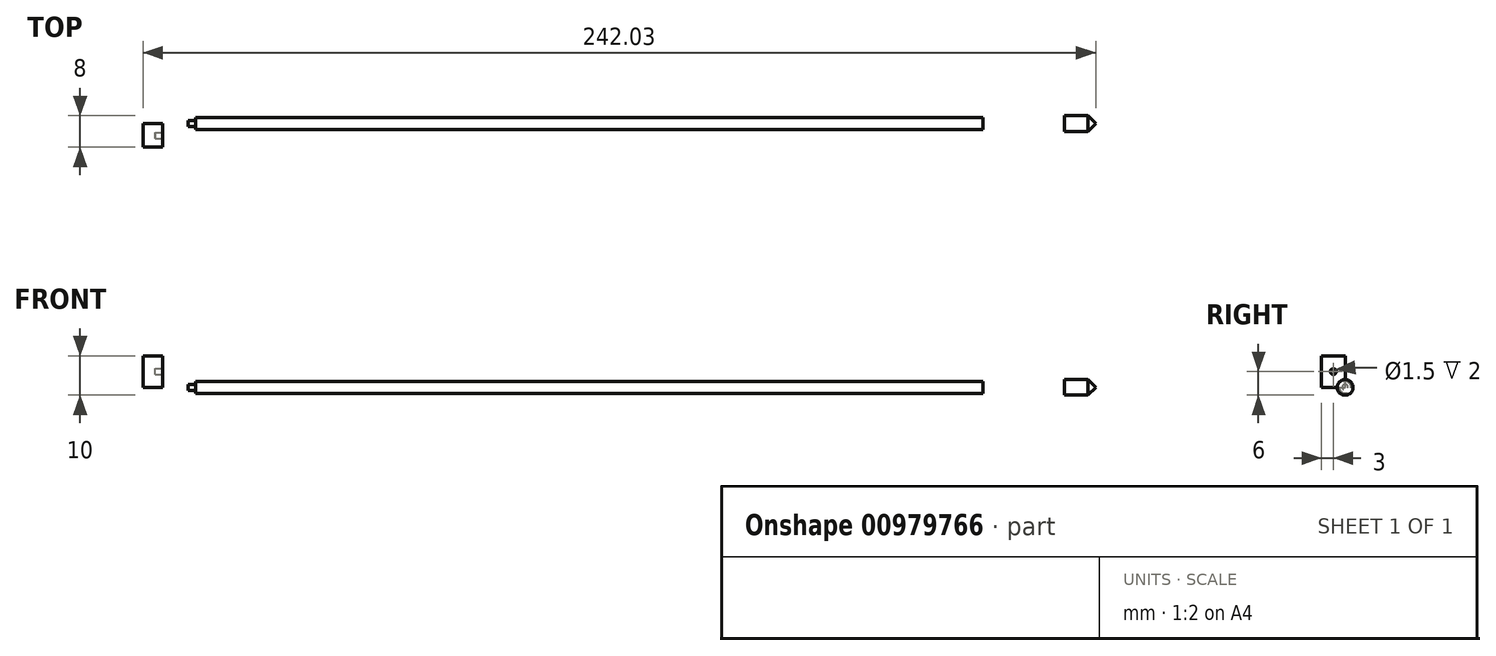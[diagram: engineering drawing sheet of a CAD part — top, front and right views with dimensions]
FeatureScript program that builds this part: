
annotation { "Feature Type Name" : "Feature", "Feature Type Description" : "" }
export const myFeature = defineFeature(function(context is Context, id is Id, definition is map)
    precondition{}
    {
        {
            var Q0;
            Q0=qCreatedBy(makeId("Front.planeOp"),FACE);
            var sketch = newSketch(context, id + "F0", { "sketchPlane" : qUnion([Q0])});
            skLineSegment(sketch, "E0.bottom", {"start": v(0, 0) * mm, "end": v(5, 0) * mm});
            skLineSegment(sketch, "E0.top", {"start": v(0, 8) * mm, "end": v(5, 8) * mm});
            skLineSegment(sketch, "E0.left", {"start": v(0, 0) * mm, "end": v(0, 8) * mm});
            skLineSegment(sketch, "E0.right", {"start": v(5, 0) * mm, "end": v(5, 8) * mm});
            skSolve(sketch);
        }
        {
            var Q0;
            Q0 = qSketchRegion(id + "F0", true);
            extrude(context, id + "F1", {"entities" : qUnion([Q0]), "depth" : 6 * mm, "offsetDistance" : 25 * mm});
        }
        {
            var Q0;
            Q0=qCreatedBy(makeId("Front.planeOp"),FACE);
            var sketch = newSketch(context, id + "F2", { "sketchPlane" : qUnion([Q0])});
            skLineSegment(sketch, "E1.bottom", {"start": v(13.38, 0) * mm, "end": v(213.38, 0) * mm});
            skLineSegment(sketch, "E1.top", {"start": v(13.38, 1.5) * mm, "end": v(213.38, 1.5) * mm});
            skLineSegment(sketch, "E1.left", {"start": v(13.38, 0) * mm, "end": v(13.38, 1.5) * mm});
            skLineSegment(sketch, "E1.right", {"start": v(213.38, 0) * mm, "end": v(213.38, 1.5) * mm});
            skSolve(sketch);
        }
        {
            var Q0;
            Q0 = qSketchRegion(id + "F2", true);
            var Q1;
            Q1=sQuery(id+"F2.wireOp",EDGE,"E1.bottom");
            revolve(context, id + "F3", {"surfaceOperationType" : NewSurfaceOperationType.NEW, "entities" : qUnion([Q0]), "axis" : qUnion([Q1]), "revolveType" : RevolveType.FULL});
        }
        {
            var Q0;
            Q0=makeQuery(id+"F3.opRevolve","SWEPT_FACE",FACE,{"disambiguationData":[OSD([sQuery(id+"F2.wireOp",EDGE,"E1.left")])]});
            var sketch = newSketch(context, id + "F4", { "sketchPlane" : qUnion([Q0])});
            skCircle(sketch, "E2", {"center": v(0, 0) * mm, "radius": 0.75 * mm});
            skSolve(sketch);
        }
        {
            var Q0;
            Q0 = qSketchRegion(id + "F4", true);
            extrude(context, id + "F5", {"entities" : qUnion([Q0]), "operationType" : NewBodyOperationType.ADD, "depth" : 2 * mm, "offsetDistance" : 25 * mm});
        }
        {
            var Q0;
            Q0=makeQuery(id+"F1.opExtrude","SWEPT_FACE",FACE,{"disambiguationData":[OSD([sQuery(id+"F0.wireOp",EDGE,"E0.right")])]});
            var sketch = newSketch(context, id + "F6", { "sketchPlane" : qUnion([Q0])});
            skCircle(sketch, "E3", {"center": v(-3, 4) * mm, "radius": 0.75 * mm});
            skPoint(sketch, "E3.centerSnap0", {"position": v(-6, 4) * mm});
            skPoint(sketch, "E3.centerSnap1", {"position": v(-3, 8) * mm});
            skSolve(sketch);
        }
        {
            var Q0;
            Q0 = qSketchRegion(id + "F6", true);
            extrude(context, id + "F7", {"entities" : qUnion([Q0]), "operationType" : NewBodyOperationType.REMOVE, "oppositeDirection" : true, "depth" : 2 * mm, "offsetDistance" : 25 * mm});
        }
        {
            var Q0;
            Q0=qCreatedBy(makeId("Front.planeOp"),FACE);
            var sketch = newSketch(context, id + "F8", { "sketchPlane" : qUnion([Q0])});
            skLineSegment(sketch, "E4", {"start": v(234.03, 0) * mm, "end": v(242.03, 0) * mm});
            skLineSegment(sketch, "E5", {"start": v(234.03, 0) * mm, "end": v(234.03, 2) * mm});
            skLineSegment(sketch, "E6", {"start": v(234.03, 2) * mm, "end": v(240.03, 2) * mm});
            skLineSegment(sketch, "E7", {"start": v(240.03, 2) * mm, "end": v(242.03, 0) * mm});
            skSolve(sketch);
        }
        {
            var Q0;
            Q0 = qSketchRegion(id + "F8", true);
            var Q1;
            Q1=sQuery(id+"F8.wireOp",EDGE,"E4");
            revolve(context, id + "F9", {"surfaceOperationType" : NewSurfaceOperationType.NEW, "entities" : qUnion([Q0]), "axis" : qUnion([Q1]), "revolveType" : RevolveType.FULL});
        }
    });
